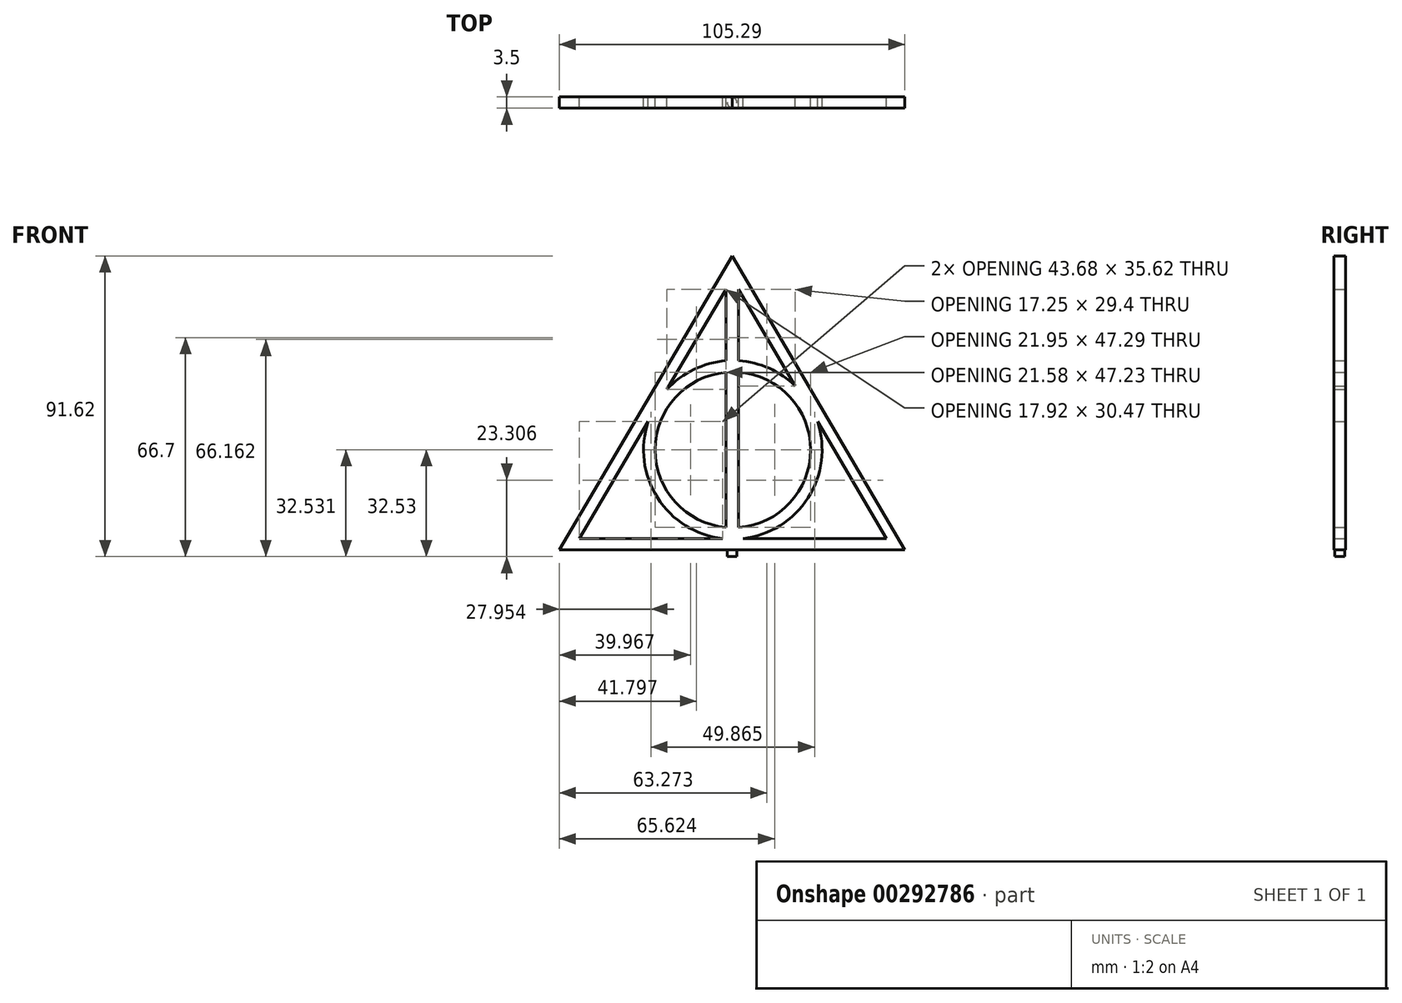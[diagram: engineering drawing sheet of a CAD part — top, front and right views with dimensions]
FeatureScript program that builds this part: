
annotation { "Feature Type Name" : "Feature", "Feature Type Description" : "" }
export const myFeature = defineFeature(function(context is Context, id is Id, definition is map)
    precondition{}
    {
        {
            var Q0;
            Q0=qCreatedBy(makeId("Front.planeOp"),FACE);
            var sketch = newSketch(context, id + "F0", { "sketchPlane" : qUnion([Q0])});
            skLineSegment(sketch, "E0", {"start": v(-9.84, 97.82) * mm, "end": v(-62.55, 8.2) * mm});
            skLineSegment(sketch, "E1", {"start": v(-62.55, 8.2) * mm, "end": v(42.74, 8.2) * mm});
            skLineSegment(sketch, "E2", {"start": v(42.74, 8.2) * mm, "end": v(-9.84, 97.82) * mm});
            skLineSegment(sketch, "E3.1", {"start": v(-56.43, 11.7) * mm, "end": v(-12.76, 11.7) * mm});
            skLineSegment(sketch, "E3.2", {"start": v(-11.8, 87.6) * mm, "end": v(-29.71, 57.13) * mm});
            skLineSegment(sketch, "E4", {"start": v(-11.8, 87.6) * mm, "end": v(-11.8, 65.86) * mm});
            skLineSegment(sketch, "E5", {"start": v(-7.9, 87.6) * mm, "end": v(-7.9, 65.88) * mm});
            skArc(sketch, "E6", {"start": v(-35.48, 47.32) * mm, "mid": v(-32.6, 24.1) * mm, "end": v(-12.76, 11.7) * mm});
            skArc(sketch, "E7.0", {"start": v(-11.8, 62.35) * mm, "mid": v(-33.37, 38.73) * mm, "end": v(-11.8, 15.12) * mm});
            skArc(sketch, "E8.trimOffspring", {"start": v(9.35, 58.2) * mm, "mid": v(1.41, 63.59) * mm, "end": v(-7.9, 65.88) * mm});
            skArc(sketch, "E9.trimOffspring", {"start": v(-11.8, 65.86) * mm, "mid": v(-21.58, 63.2) * mm, "end": v(-29.71, 57.13) * mm});
            skArc(sketch, "E10.trimOffspring", {"start": v(-7.9, 15.09) * mm, "mid": v(14.05, 38.73) * mm, "end": v(-7.9, 62.38) * mm});
            skLineSegment(sketch, "E11.trimOffspring", {"start": v(-35.48, 47.32) * mm, "end": v(-56.43, 11.7) * mm});
            skLineSegment(sketch, "E12.trimOffspring", {"start": v(-11.8, 62.35) * mm, "end": v(-11.8, 15.12) * mm});
            skLineSegment(sketch, "E13.trimOffspring", {"start": v(-7.9, 62.38) * mm, "end": v(-7.9, 15.09) * mm});
            skLineSegment(sketch, "E14.trimOffspring", {"start": v(9.35, 58.2) * mm, "end": v(-7.9, 87.6) * mm});
            skLineSegment(sketch, "E15", {"start": v(-9.66, 38.73) * mm, "end": v(-9.66, -11.88) * mm, "construction": true});
            skLineSegment(sketch, "E16.MirrorCS", {"start": v(16.16, 47.32) * mm, "end": v(37.1, 11.7) * mm});
            skLineSegment(sketch, "E17.MirrorCS", {"start": v(37.1, 11.7) * mm, "end": v(-6.57, 11.7) * mm});
            skArc(sketch, "E18.MirrorCS", {"start": v(16.16, 47.32) * mm, "mid": v(13.28, 24.1) * mm, "end": v(-6.57, 11.7) * mm});
            skSolve(sketch);
        }
        {
            var Q0;
            Q0=makeQuery(id+"F0.imprint","IMPRINT",FACE,{"disambiguationData":[TD([[makeQuery(id+"F0.imprint","IMPRINT",EDGE,{"derivedFrom":sQuery(id+"F0.wireOp",EDGE,"E0")}),1.0]])]});
            var Q1;
            {var subQ5=sQuery(id+"F0.wireOp",EDGE,"E6");Q1=makeQuery(id+"F0.imprint","IMPRINT",FACE,{"disambiguationData":[TD([[makeQuery(id+"F0.imprint","IMPRINT",EDGE,{"derivedFrom":subQ5}),1.0]])]});}
            var Q2;
            {var subQ4=sQuery(id+"F0.wireOp",EDGE,"E3.0");var subQ11=sQuery(id+"F0.wireOp",EDGE,"E3.2");var subQ12=makeQuery(id+"F0.imprint","INTERSECT",VERTEX,{"derivedFrom":[subQ4,subQ11]});Q2=makeQuery(id+"F0.imprint","IMPRINT",FACE,{"disambiguationData":[TD([[makeQuery(id+"F0.imprint","IMPRINT",EDGE,{"disambiguationData":[TD([[subQ12,1.0]])],"derivedFrom":subQ4}),1.0]])]});}
            var Q3;
            {var subQ5=sQuery(id+"F0.wireOp",EDGE,"E8.trimOffspring");Q3=makeQuery(id+"F0.imprint","IMPRINT",FACE,{"disambiguationData":[TD([[makeQuery(id+"F0.imprint","IMPRINT",EDGE,{"derivedFrom":subQ5}),1.0]])]});}
            extrude(context, id + "F1", {"entities" : qUnion([Q0, Q1, Q2, Q3]), "depth" : 3.5 * mm});
        }
        {
            var Q0;
            Q0=makeQuery(id+"F1.opExtrude","SWEPT_FACE",FACE,{"disambiguationData":[OSD([sQuery(id+"F0.wireOp",EDGE,"E1")])]});
            var sketch = newSketch(context, id + "F2", { "sketchPlane" : qUnion([Q0])});
            skLineSegment(sketch, "E19", {"start": v(-9.9, 3.5) * mm, "end": v(-9.9, 0) * mm, "construction": true});
            skCircle(sketch, "E20", {"center": v(-9.9, 1.75) * mm, "radius": 1.5 * mm});
            skSolve(sketch);
        }
        {
            var Q0;
            Q0 = qSketchRegion(id + "F2", true);
            extrude(context, id + "F3", {"entities" : qUnion([Q0]), "operationType" : NewBodyOperationType.ADD, "depth" : 2 * mm});
        }
    });
